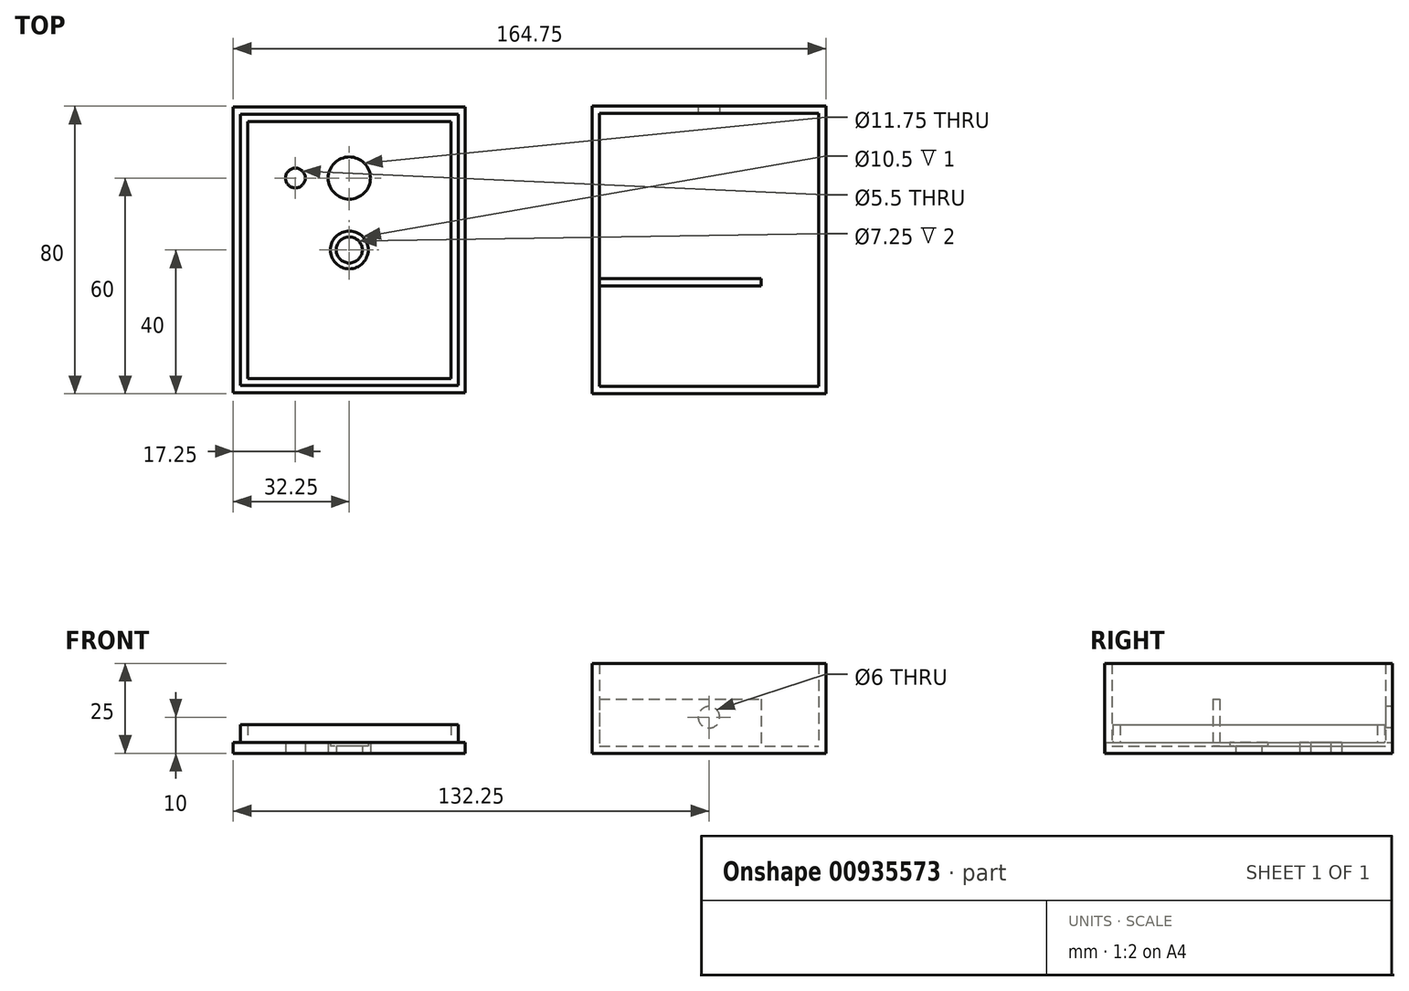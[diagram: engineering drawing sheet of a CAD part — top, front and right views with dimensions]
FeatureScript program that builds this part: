
annotation { "Feature Type Name" : "Feature", "Feature Type Description" : "" }
export const myFeature = defineFeature(function(context is Context, id is Id, definition is map)
    precondition{}
    {
        {
            var Q0;
            Q0=qCreatedBy(makeId("Top.planeOp"),FACE);
            var sketch = newSketch(context, id + "F0", { "sketchPlane" : qUnion([Q0])});
            skLineSegment(sketch, "E0.bottom", {"start": v(-32.5, -40) * mm, "end": v(32.5, -40) * mm});
            skLineSegment(sketch, "E0.top", {"start": v(-32.5, 40) * mm, "end": v(32.5, 40) * mm});
            skLineSegment(sketch, "E0.left", {"start": v(-32.5, -40) * mm, "end": v(-32.5, 40) * mm});
            skLineSegment(sketch, "E0.right", {"start": v(32.5, -40) * mm, "end": v(32.5, 40) * mm});
            skPoint(sketch, "E0.middle", {"position": v(0, 0) * mm});
            skLineSegment(sketch, "E1.0", {"start": v(-30.5, 38) * mm, "end": v(30.5, 38) * mm});
            skLineSegment(sketch, "E1.1", {"start": v(-30.5, -38) * mm, "end": v(-30.5, 38) * mm});
            skLineSegment(sketch, "E1.2", {"start": v(-30.5, -38) * mm, "end": v(30.5, -38) * mm});
            skLineSegment(sketch, "E1.3", {"start": v(30.5, -38) * mm, "end": v(30.5, 38) * mm});
            skLineSegment(sketch, "E2.bottom", {"start": v(-30.5, -8) * mm, "end": v(14.5, -8) * mm});
            skLineSegment(sketch, "E2.top", {"start": v(-30.5, -10) * mm, "end": v(14.5, -10) * mm});
            skLineSegment(sketch, "E2.left", {"start": v(-30.5, -8) * mm, "end": v(-30.5, -10) * mm});
            skLineSegment(sketch, "E2.right", {"start": v(14.5, -8) * mm, "end": v(14.5, -10) * mm});
            skLineSegment(sketch, "E3.bottom", {"start": v(-69.75, -37.75) * mm, "end": v(-130.25, -37.75) * mm});
            skLineSegment(sketch, "E3.top", {"start": v(-69.75, 37.75) * mm, "end": v(-130.25, 37.75) * mm});
            skLineSegment(sketch, "E3.left", {"start": v(-69.75, -37.75) * mm, "end": v(-69.75, 37.75) * mm});
            skLineSegment(sketch, "E3.right", {"start": v(-130.25, -37.75) * mm, "end": v(-130.25, 37.75) * mm});
            skPoint(sketch, "E3.middle", {"position": v(-100, 0) * mm});
            skLineSegment(sketch, "E4.0", {"start": v(-67.75, 39.75) * mm, "end": v(-132.25, 39.75) * mm});
            skLineSegment(sketch, "E4.1", {"start": v(-67.75, -39.75) * mm, "end": v(-67.75, 39.75) * mm});
            skLineSegment(sketch, "E4.2", {"start": v(-67.75, -39.75) * mm, "end": v(-132.25, -39.75) * mm});
            skLineSegment(sketch, "E4.3", {"start": v(-132.25, -39.75) * mm, "end": v(-132.25, 39.75) * mm});
            skLineSegment(sketch, "E5.0", {"start": v(-71.75, 35.75) * mm, "end": v(-128.25, 35.75) * mm});
            skLineSegment(sketch, "E5.1", {"start": v(-71.75, -35.75) * mm, "end": v(-71.75, 35.75) * mm});
            skLineSegment(sketch, "E5.2", {"start": v(-71.75, -35.75) * mm, "end": v(-128.25, -35.75) * mm});
            skLineSegment(sketch, "E5.3", {"start": v(-128.25, -35.75) * mm, "end": v(-128.25, 35.75) * mm});
            skCircle(sketch, "E6", {"center": v(-100, 20) * mm, "radius": 5.88 * mm});
            skCircle(sketch, "E7", {"center": v(-100, 0) * mm, "radius": 3.62 * mm});
            skCircle(sketch, "E8", {"center": v(-100, 0) * mm, "radius": 5.25 * mm});
            skCircle(sketch, "E9", {"center": v(-115, 20) * mm, "radius": 2.75 * mm});
            skSolve(sketch);
        }
        {
            var Q0;
            {var subQ3=sQuery(id+"F0.wireOp",EDGE,"E1.0");Q0=makeQuery(id+"F0.imprint","IMPRINT",FACE,{"disambiguationData":[TD([[makeQuery(id+"F0.imprint","IMPRINT",EDGE,{"derivedFrom":subQ3}),-1.0]])]});}
            extrude(context, id + "F1", {"entities" : qUnion([Q0]), "depth" : 2 * mm, "offsetDistance" : 25 * mm});
        }
        {
            var Q0;
            Q0=makeQuery(id+"F0.imprint","IMPRINT",FACE,{"disambiguationData":[TD([[makeQuery(id+"F0.imprint","IMPRINT",EDGE,{"derivedFrom":sQuery(id+"F0.wireOp",EDGE,"E0.bottom")}),1.0]])]});
            extrude(context, id + "F2", {"entities" : qUnion([Q0]), "operationType" : NewBodyOperationType.ADD, "depth" : 25 * mm, "offsetDistance" : 25 * mm});
        }
        {
            var Q0;
            {var subQ0=sQuery(id+"F0.wireOp",EDGE,"E2.bottom");Q0=makeQuery(id+"F0.imprint","IMPRINT",FACE,{"disambiguationData":[TD([[makeQuery(id+"F0.imprint","IMPRINT",EDGE,{"derivedFrom":subQ0}),-1.0]])]});}
            extrude(context, id + "F3", {"entities" : qUnion([Q0]), "operationType" : NewBodyOperationType.ADD, "depth" : 15 * mm, "offsetDistance" : 25 * mm});
        }
        {
            var Q0;
            Q0=makeQuery(id+"F0.imprint","IMPRINT",FACE,{"disambiguationData":[TD([[makeQuery(id+"F0.imprint","IMPRINT",EDGE,{"derivedFrom":sQuery(id+"F0.wireOp",EDGE,"E5.0")}),1.0]])]});
            var Q1;
            Q1=makeQuery(id+"F0.imprint","IMPRINT",FACE,{"disambiguationData":[TD([[makeQuery(id+"F0.imprint","IMPRINT",EDGE,{"derivedFrom":sQuery(id+"F0.wireOp",EDGE,"E3.bottom")}),1.0]])]});
            extrude(context, id + "F4", {"entities" : qUnion([Q0, Q1]), "depth" : 3 * mm, "offsetDistance" : 25 * mm});
        }
        {
            var Q0;
            Q0=makeQuery(id+"F0.imprint","IMPRINT",FACE,{"disambiguationData":[TD([[makeQuery(id+"F0.imprint","IMPRINT",EDGE,{"derivedFrom":sQuery(id+"F0.wireOp",EDGE,"E3.bottom")}),-1.0]])]});
            extrude(context, id + "F5", {"entities" : qUnion([Q0]), "operationType" : NewBodyOperationType.ADD, "depth" : 8 * mm, "offsetDistance" : 25 * mm});
        }
        {
            var Q0;
            Q0=makeQuery(id+"F0.imprint","IMPRINT",FACE,{"disambiguationData":[TD([[makeQuery(id+"F0.imprint","IMPRINT",EDGE,{"derivedFrom":sQuery(id+"F0.wireOp",EDGE,"E7")}),-1.0]])]});
            extrude(context, id + "F6", {"entities" : qUnion([Q0]), "operationType" : NewBodyOperationType.ADD, "depth" : 2 * mm, "offsetDistance" : 25 * mm});
        }
        {
            var Q0;
            Q0=qCreatedBy(makeId("Front.planeOp"),FACE);
            var sketch = newSketch(context, id + "F7", { "sketchPlane" : qUnion([Q0])});
            skCircle(sketch, "E10", {"center": v(0, 10) * mm, "radius": 3 * mm});
            skSolve(sketch);
        }
        {
            var Q0;
            Q0=makeQuery(id+"F7.imprint","IMPRINT",FACE,{"disambiguationData":[TD([[makeQuery(id+"F7.imprint","IMPRINT",EDGE,{"derivedFrom":sQuery(id+"F7.wireOp",EDGE,"E10")}),1.0]])]});
            extrude(context, id + "F8", {"entities" : qUnion([Q0]), "operationType" : NewBodyOperationType.REMOVE, "oppositeDirection" : true, "depth" : 47.8 * mm, "offsetDistance" : 25 * mm});
        }
    });
